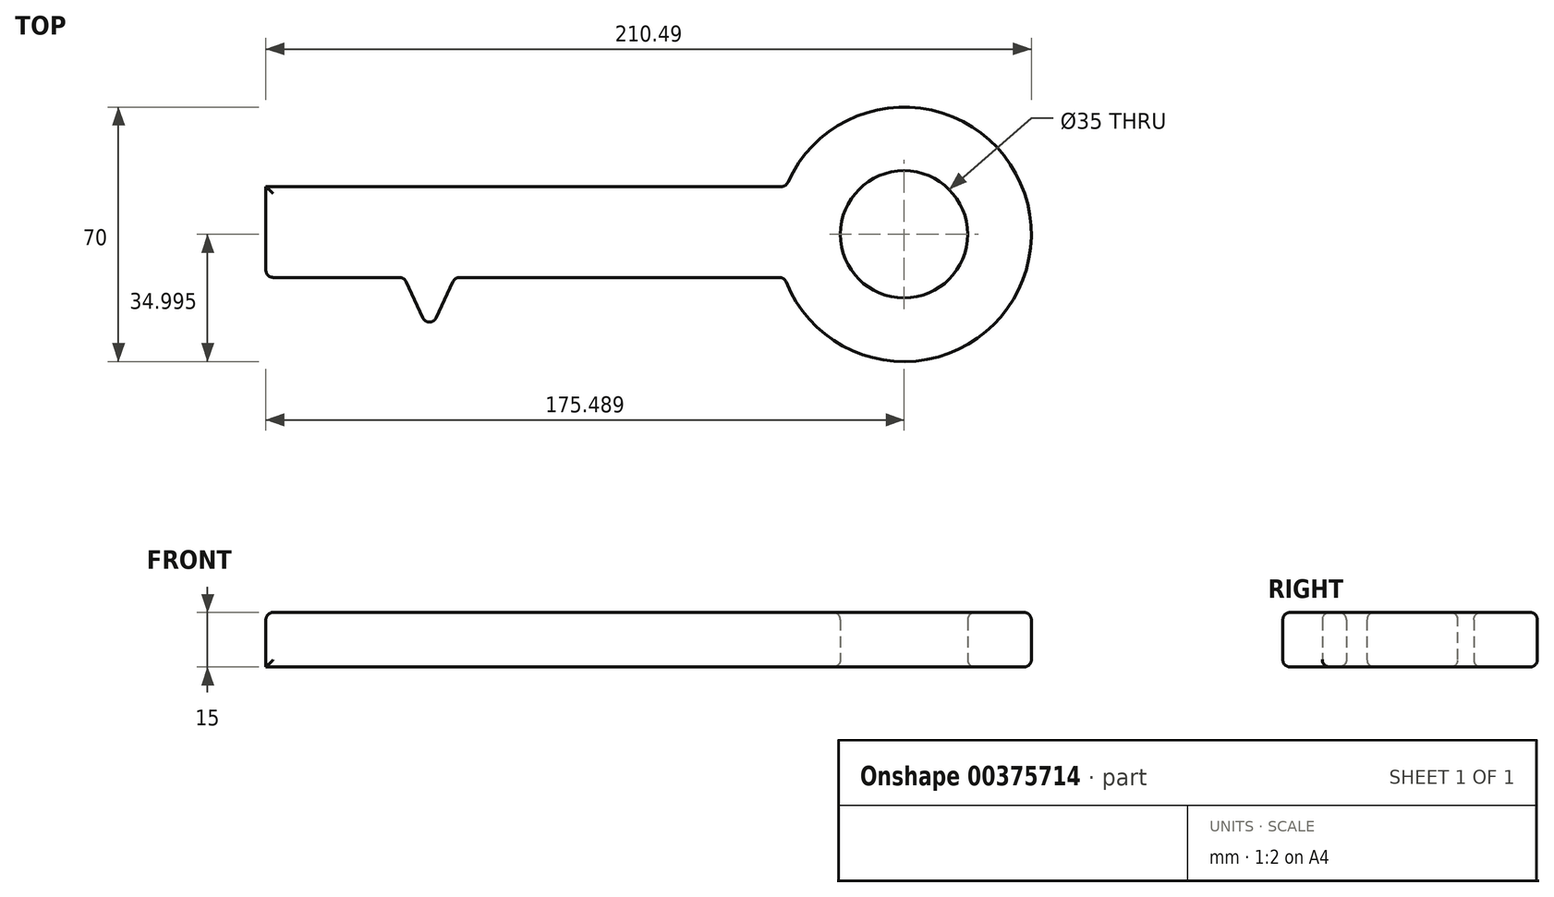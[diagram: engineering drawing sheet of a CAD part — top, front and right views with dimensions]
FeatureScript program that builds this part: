
annotation { "Feature Type Name" : "Feature", "Feature Type Description" : "" }
export const myFeature = defineFeature(function(context is Context, id is Id, definition is map)
    precondition{}
    {
        {
            var Q0;
            Q0=qCreatedBy(makeId("Top.planeOp"),FACE);
            var sketch = newSketch(context, id + "F0", { "sketchPlane" : qUnion([Q0])});
            skLineSegment(sketch, "E0.bottom", {"start": v(68.46, 25) * mm, "end": v(-74.59, 25) * mm});
            skLineSegment(sketch, "E0.top", {"start": v(67.97, 0) * mm, "end": v(-74.59, 0) * mm});
            skLineSegment(sketch, "E0.right", {"start": v(-74.59, 25) * mm, "end": v(-74.59, 0) * mm});
            skLineSegment(sketch, "E1.bottom", {"start": v(-74.59, 0) * mm, "end": v(-64.59, 0) * mm});
            skLineSegment(sketch, "E1.top", {"start": v(-74.59, -30) * mm, "end": v(-64.59, -30) * mm});
            skLineSegment(sketch, "E1.left", {"start": v(-74.59, 0) * mm, "end": v(-74.59, -30) * mm});
            skLineSegment(sketch, "E1.right", {"start": v(-64.59, 0) * mm, "end": v(-64.59, -30) * mm});
            skLineSegment(sketch, "E2.bottom", {"start": v(-54.59, 0) * mm, "end": v(-46.59, 0) * mm});
            skLineSegment(sketch, "E2.top", {"start": v(-54.59, -15) * mm, "end": v(-46.59, -15) * mm});
            skLineSegment(sketch, "E2.left", {"start": v(-54.59, 0) * mm, "end": v(-54.59, -15) * mm});
            skLineSegment(sketch, "E2.right", {"start": v(-46.59, 0) * mm, "end": v(-46.59, -15) * mm});
            skLineSegment(sketch, "E3", {"start": v(-36.59, 0) * mm, "end": v(-29.59, -15) * mm});
            skLineSegment(sketch, "E4", {"start": v(-29.59, -15) * mm, "end": v(-22.58, 0) * mm});
            skPoint(sketch, "E5.orphan", {"position": v(80.21, 0) * mm});
            skPoint(sketch, "E0.left.start.orphan", {"position": v(80.21, 25) * mm});
            skArc(sketch, "E6", {"start": v(67.97, 0) * mm, "mid": v(135.9, 11.16) * mm, "end": v(68.46, 25) * mm});
            skCircle(sketch, "E7", {"center": v(100.9, 11.86) * mm, "radius": 17.5 * mm});
            skSolve(sketch);
        }
        {
            var Q0;
            Q0=makeQuery(id+"F0.imprint","IMPRINT",FACE,{"disambiguationData":[TD([[makeQuery(id+"F0.imprint","IMPRINT",EDGE,{"derivedFrom":sQuery(id+"F0.wireOp",EDGE,"E0.bottom")}),1.0]])]});
            var Q1;
            {var subQ0=sQuery(id+"F0.wireOp",EDGE,"E3");Q1=makeQuery(id+"F0.imprint","IMPRINT",FACE,{"disambiguationData":[TD([[makeQuery(id+"F0.imprint","IMPRINT",EDGE,{"derivedFrom":subQ0}),1.0]])]});}
            var Q2;
            Q2=makeQuery(id+"F0.imprint","IMPRINT",FACE,{"disambiguationData":[TD([[makeQuery(id+"F0.imprint","IMPRINT",EDGE,{"derivedFrom":sQuery(id+"F0.wireOp",EDGE,"E2.bottom")}),-1.0]])]});
            var Q3;
            Q3=makeQuery(id+"F0.imprint","IMPRINT",FACE,{"disambiguationData":[TD([[makeQuery(id+"F0.imprint","IMPRINT",EDGE,{"derivedFrom":sQuery(id+"F0.wireOp",EDGE,"E1.bottom")}),-1.0]])]});
            extrude(context, id + "F1", {"entities" : qUnion([Q0, Q1, Q2, Q3]), "depth" : 15 * mm});
        }
        {
            var Q0;
            Q0=makeQuery(id+"F1.opExtrude","CAP_EDGE",EDGE,{"disambiguationData":[OSD([sQuery(id+"F0.wireOp",EDGE,"E0.bottom")])],"isStart":false});
            var Q1;
            Q1=makeQuery(id+"F1.opExtrude","CAP_EDGE",EDGE,{"disambiguationData":[OSD([sQuery(id+"F0.wireOp",EDGE,"E6")])],"isStart":false});
            var Q2;
            Q2=makeQuery(id+"F1.opExtrude","CAP_EDGE",EDGE,{"disambiguationData":[OSD([sQuery(id+"F0.wireOp",EDGE,"E4")])],"isStart":false});
            var Q3;
            Q3=makeQuery(id+"F1.opExtrude","CAP_EDGE",EDGE,{"disambiguationData":[OSD([sQuery(id+"F0.wireOp",EDGE,"E2.right")])],"isStart":false});
            var Q4;
            Q4=makeQuery(id+"F1.opExtrude","CAP_FACE",FACE,{"disambiguationData":[OSD([sQuery(id+"F0.wireOp",EDGE,"E0.bottom"),sQuery(id+"F0.wireOp",EDGE,"E0.top"),sQuery(id+"F0.wireOp",EDGE,"E0.right"),sQuery(id+"F0.wireOp",EDGE,"E1.top"),sQuery(id+"F0.wireOp",EDGE,"E1.left"),sQuery(id+"F0.wireOp",EDGE,"E1.right"),sQuery(id+"F0.wireOp",EDGE,"E2.top"),sQuery(id+"F0.wireOp",EDGE,"E2.left"),sQuery(id+"F0.wireOp",EDGE,"E2.right"),sQuery(id+"F0.wireOp",EDGE,"E3"),sQuery(id+"F0.wireOp",EDGE,"E4"),sQuery(id+"F0.wireOp",EDGE,"E6"),sQuery(id+"F0.wireOp",EDGE,"E7")])],"isStart":false});
            var Q5;
            Q5=makeQuery(id+"F1.opExtrude","SWEPT_EDGE",EDGE,{"disambiguationData":[OSD([sQuery(id+"F0.wireOp",EDGE,"E2.top"),sQuery(id+"F0.wireOp",EDGE,"E2.right")])]});
            var Q6;
            {var subQ0=sQuery(id+"F0.wireOp",EDGE,"E0.top");Q6=makeQuery(id+"F1.opExtrude","CAP_EDGE",EDGE,{"disambiguationData":[OSD([subQ0]),TDD([makeQuery(id+"F0.imprint","IMPRINT",EDGE,{"disambiguationData":[TD([[makeQuery(id+"F0.imprint","INTERSECT",VERTEX,{"derivedFrom":[subQ0,sQuery(id+"F0.wireOp",EDGE,"E3")]}),-1.0]])],"derivedFrom":subQ0})])],"isStart":true});}
            var Q7;
            Q7=makeQuery(id+"F1.opExtrude","CAP_EDGE",EDGE,{"disambiguationData":[OSD([sQuery(id+"F0.wireOp",EDGE,"E3")])],"isStart":true});
            var Q8;
            {var subQ0=sQuery(id+"F0.wireOp",EDGE,"E0.top");Q8=makeQuery(id+"F1.opExtrude","CAP_EDGE",EDGE,{"disambiguationData":[OSD([subQ0]),TDD([makeQuery(id+"F0.imprint","IMPRINT",EDGE,{"disambiguationData":[TD([[makeQuery(id+"F0.imprint","INTERSECT",VERTEX,{"derivedFrom":[subQ0,sQuery(id+"F0.wireOp",EDGE,"E6")]}),-1.0]])],"derivedFrom":subQ0})])],"isStart":true});}
            var Q9;
            Q9=makeQuery(id+"F1.opExtrude","SWEPT_EDGE",EDGE,{"disambiguationData":[OSD([sQuery(id+"F0.wireOp",EDGE,"E1.top"),sQuery(id+"F0.wireOp",EDGE,"E1.left")])]});
            var Q10;
            Q10=makeQuery(id+"F1.opExtrude","SWEPT_EDGE",EDGE,{"disambiguationData":[OSD([sQuery(id+"F0.wireOp",EDGE,"E2.top"),sQuery(id+"F0.wireOp",EDGE,"E2.left")])]});
            var Q11;
            {var subQ0=sQuery(id+"F0.wireOp",EDGE,"E0.top");Q11=makeQuery(id+"F1.opExtrude","CAP_EDGE",EDGE,{"disambiguationData":[OSD([subQ0]),TDD([makeQuery(id+"F0.imprint","IMPRINT",EDGE,{"disambiguationData":[TD([[makeQuery(id+"F0.imprint","INTERSECT",VERTEX,{"derivedFrom":[subQ0,sQuery(id+"F0.wireOp",EDGE,"E1.bottom"),sQuery(id+"F0.wireOp",EDGE,"E1.right")]}),1.0]])],"derivedFrom":subQ0})])],"isStart":true});}
            var Q12;
            Q12=makeQuery(id+"F1.opExtrude","CAP_EDGE",EDGE,{"disambiguationData":[OSD([sQuery(id+"F0.wireOp",EDGE,"E7")])],"isStart":true});
            var Q13;
            Q13=makeQuery(id+"F1.opExtrude","CAP_EDGE",EDGE,{"disambiguationData":[OSD([sQuery(id+"F0.wireOp",EDGE,"E0.bottom")])],"isStart":true});
            var Q14;
            Q14=makeQuery(id+"F1.opExtrude","CAP_EDGE",EDGE,{"disambiguationData":[OSD([sQuery(id+"F0.wireOp",EDGE,"E4")])],"isStart":true});
            var Q15;
            Q15=makeQuery(id+"F1.opExtrude","CAP_EDGE",EDGE,{"disambiguationData":[OSD([sQuery(id+"F0.wireOp",EDGE,"E2.top")])],"isStart":true});
            var Q16;
            Q16=makeQuery(id+"F1.opExtrude","CAP_EDGE",EDGE,{"disambiguationData":[OSD([sQuery(id+"F0.wireOp",EDGE,"E1.top")])],"isStart":true});
            var Q17;
            Q17=makeQuery(id+"F1.opExtrude","CAP_EDGE",EDGE,{"disambiguationData":[OSD([sQuery(id+"F0.wireOp",EDGE,"E6")])],"isStart":true});
            var Q18;
            Q18=makeQuery(id+"F1.opExtrude","SWEPT_FACE",FACE,{"disambiguationData":[OSD([sQuery(id+"F0.wireOp",EDGE,"E4")])]});
            var Q19;
            Q19=makeQuery(id+"F1.opExtrude","SWEPT_FACE",FACE,{"disambiguationData":[OSD([sQuery(id+"F0.wireOp",EDGE,"E1.right")])]});
            var Q20;
            Q20=makeQuery(id+"F1.opExtrude","SWEPT_EDGE",EDGE,{"disambiguationData":[OSD([sQuery(id+"F0.wireOp",EDGE,"E0.top"),sQuery(id+"F0.wireOp",EDGE,"E4")])]});
            var Q21;
            Q21=makeQuery(id+"F1.opExtrude","SWEPT_EDGE",EDGE,{"disambiguationData":[OSD([sQuery(id+"F0.wireOp",EDGE,"E3"),sQuery(id+"F0.wireOp",EDGE,"E4")])]});
            var Q22;
            Q22=makeQuery(id+"F1.opExtrude","SWEPT_EDGE",EDGE,{"disambiguationData":[OSD([sQuery(id+"F0.wireOp",EDGE,"E0.top"),sQuery(id+"F0.wireOp",EDGE,"E3")])]});
            var Q23;
            Q23=makeQuery(id+"F1.opExtrude","SWEPT_EDGE",EDGE,{"disambiguationData":[OSD([sQuery(id+"F0.wireOp",EDGE,"E1.top"),sQuery(id+"F0.wireOp",EDGE,"E1.right")])]});
            var Q24;
            {var subQ0=sQuery(id+"F0.wireOp",EDGE,"E0.top");Q24=makeQuery(id+"F1.opExtrude","SWEPT_FACE",FACE,{"disambiguationData":[OSD([subQ0]),TDD([makeQuery(id+"F0.imprint","IMPRINT",EDGE,{"disambiguationData":[TD([[makeQuery(id+"F0.imprint","INTERSECT",VERTEX,{"derivedFrom":[subQ0,sQuery(id+"F0.wireOp",EDGE,"E1.bottom"),sQuery(id+"F0.wireOp",EDGE,"E1.right")]}),1.0]])],"derivedFrom":subQ0})])]});}
            var Q25;
            Q25=makeQuery(id+"F1.opExtrude","SWEPT_FACE",FACE,{"disambiguationData":[OSD([sQuery(id+"F0.wireOp",EDGE,"E1.top")])]});
            var Q26;
            Q26=makeQuery(id+"F1.opExtrude","SWEPT_FACE",FACE,{"disambiguationData":[OSD([sQuery(id+"F0.wireOp",EDGE,"E2.top")])]});
            var Q27;
            Q27=makeQuery(id+"F1.opExtrude","SWEPT_EDGE",EDGE,{"disambiguationData":[OSD([sQuery(id+"F0.wireOp",EDGE,"E0.bottom"),sQuery(id+"F0.wireOp",EDGE,"E6")])]});
            var Q28;
            Q28=makeQuery(id+"F1.opExtrude","SWEPT_FACE",FACE,{"disambiguationData":[OSD([sQuery(id+"F0.wireOp",EDGE,"E6")])]});
            fillet(context, id + "F2", {"entities" : qUnion([Q0, Q1, Q2, Q3, Q4, Q5, Q6, Q7, Q8, Q9, Q10, Q11, Q12, Q13, Q14, Q15, Q16, Q17, Q18, Q19, Q20, Q21, Q22, Q23, Q24, Q25, Q26, Q27, Q28]), "radius" : 2 * mm, "tangentPropagation" : true, "allowEdgeOverflow" : false});
        }
    });
